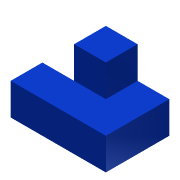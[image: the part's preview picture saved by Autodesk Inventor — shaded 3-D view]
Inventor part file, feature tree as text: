
AUTODESK INVENTOR PART (.ipt)
format: ipt  version: 2015 (Build 190159000, 159)  size: 94,720 bytes
history: native  units: in
note: dims shown in document units (in); Inventor stores cm internally (conversion verified against a paired STEP export)
features: extrude x2, sketch x2
ambient origin geometry x8: Origin, YZ Plane, XZ Plane, XY Plane, X Axis, Y Axis, Z Axis, Center Point
bodies: Solid1 (feature_tree)
feature tree (4):
  extrude  "Extrusion1"  Depth=1.0in
  extrude  "Extrusion2"  Depth=1.0in
  sketch  "Sketch1"  dims[d0=3.0in d1=1.0in]
  sketch  "Sketch2"  dims[d2=1.0in d3=1.0in d4=2.0in d5=1.0in d6=0.0in d7=1.0in d8=1.0in d9=0.0in]
